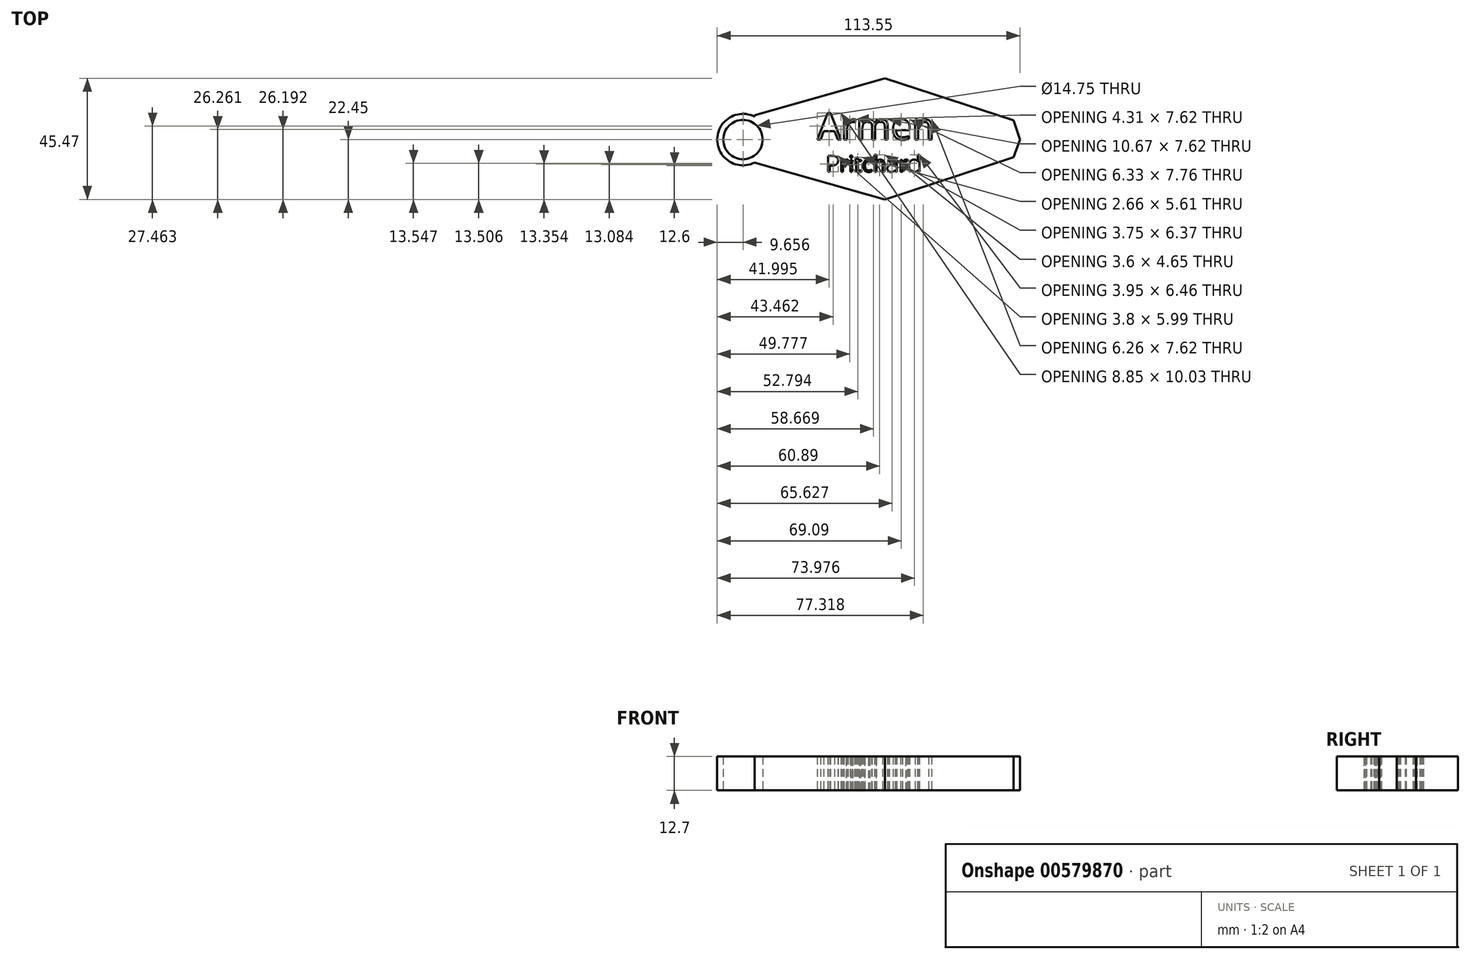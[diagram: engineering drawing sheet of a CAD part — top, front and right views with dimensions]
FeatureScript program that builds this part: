
annotation { "Feature Type Name" : "Feature", "Feature Type Description" : "" }
export const myFeature = defineFeature(function(context is Context, id is Id, definition is map)
    precondition{}
    {
        {
            var Q0;
            Q0=qCreatedBy(makeId("Top.planeOp"),FACE);
            var sketch = newSketch(context, id + "F0", { "sketchPlane" : qUnion([Q0])});
            skLineSegment(sketch, "E0", {"start": v(0, 23.02) * mm, "end": v(-48.88, 9.18) * mm});
            skLineSegment(sketch, "E1", {"start": v(0, 23.02) * mm, "end": v(48.27, 7.2) * mm});
            skCircle(sketch, "E2", {"center": v(-53.24, 0) * mm, "radius": 9.65 * mm});
            skLineSegment(sketch, "E3", {"start": v(-48.88, -8.6) * mm, "end": v(0, -22.45) * mm});
            skPoint(sketch, "E4.end.orphan", {"position": v(48.27, -8.35) * mm});
            skLineSegment(sketch, "E5", {"start": v(0, -22.45) * mm, "end": v(48.27, -6.63) * mm});
            skCircle(sketch, "E6", {"center": v(-53.24, 0) * mm, "radius": 7.38 * mm});
            skPoint(sketch, "E7.end.orphan", {"position": v(68.48, 0) * mm});
            skLineSegment(sketch, "E8", {"start": v(48.27, -6.63) * mm, "end": v(50.65, 0) * mm});
            skLineSegment(sketch, "E9", {"start": v(50.65, 0) * mm, "end": v(48.27, 7.2) * mm});
            skText(sketch, "E10", { "text": "Armen", "fontName": "OpenSans-Regular.ttf"});
            skText(sketch, "E11", { "text": "Pritchard\n", "fontName": "OpenSans-Regular.ttf"});
            skLineSegment(sketch, "E12", {"start": v(-48.88, -8.6) * mm, "end": v(-48.88, 9.18) * mm});
            const initialGuessF0  = {"E10": [-0.02533, 0, 1, 0, 0.01007], "E11": [-0.02216, -0.01209, 1, 0, 0.00604]};
            skSetInitialGuess(sketch, initialGuessF0);
            skSolve(sketch);
        }
        {
            var Q0;
            Q0 = qSketchRegion(id + "F0", true);
            extrude(context, id + "F1", {"entities" : qUnion([Q0]), "depth" : 12.7 * mm, "offsetDistance" : 25.4 * mm});
        }
    });
